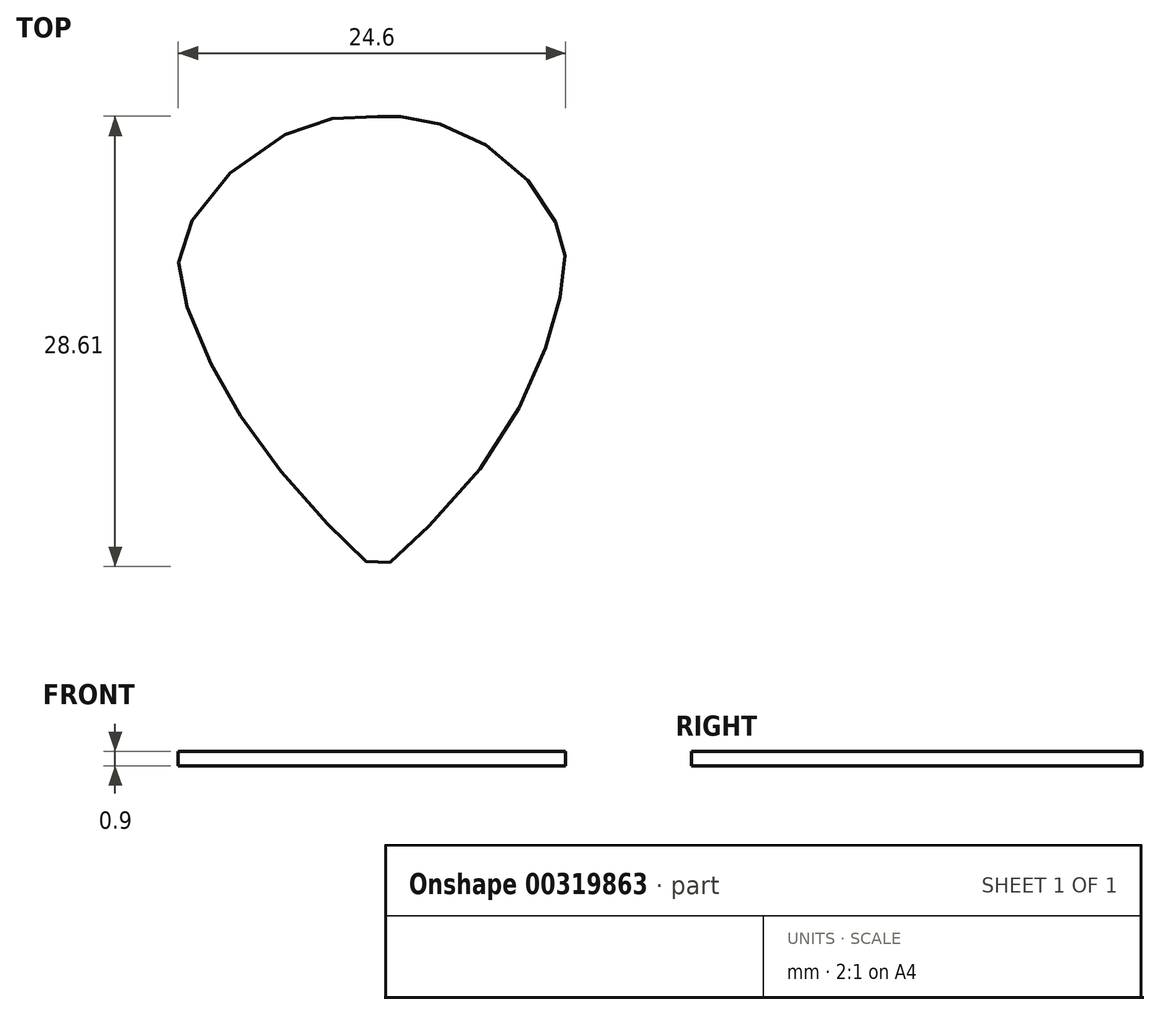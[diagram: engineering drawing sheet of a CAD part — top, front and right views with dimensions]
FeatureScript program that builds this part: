
annotation { "Feature Type Name" : "Feature", "Feature Type Description" : "" }
export const myFeature = defineFeature(function(context is Context, id is Id, definition is map)
    precondition{}
    {
        {
            var Q0;
            Q0=qCreatedBy(makeId("Top.planeOp"),FACE);
            var sketch = newSketch(context, id + "F0", { "sketchPlane" : qUnion([Q0])});
            skFitSpline(sketch, "E0", {"points": [v(0, 16.79) * mm, v(3.07, 16.79) * mm], "startDerivative": vector(3.07, 0) * mm, "endDerivative": vector(3.07, 0) * mm});
            skFitSpline(sketch, "E1", {"points": [v(0, 16.79) * mm, v(1.47, 16.79) * mm, v(2.93, 16.58) * mm, v(4.5, 16.12) * mm, v(6.77, 15.05) * mm, v(9.08, 13.24) * mm, v(10.58, 11.37) * mm, v(11.54, 9.58) * mm, v(11.8, 8.7) * mm, v(11.95, 7.34) * mm, v(11.67, 5.65) * mm, v(11.23, 3.75) * mm, v(9.95, 0.34) * mm, v(8.07, -3.36) * mm, v(4.7, -7.75) * mm, v(1.7, -10.68) * mm, v(0.56, -11.67) * mm, v(0, -11.79) * mm, v(-0.49, -11.63) * mm, v(-1.4, -10.86) * mm, v(-4.22, -7.96) * mm, v(-7.05, -4.55) * mm, v(-9.42, -1.1) * mm, v(-10.87, 1.7) * mm, v(-12.2, 5.04) * mm, v(-12.65, 6.96) * mm, v(-12.5, 8.35) * mm, v(-11.72, 10.31) * mm, v(-9.57, 12.98) * mm, v(-6.15, 15.5) * mm, v(-3.54, 16.47) * mm, v(-2.2, 16.79) * mm, v(0, 16.79) * mm]});
            skSolve(sketch);
        }
        {
            var Q0;
            Q0 = qSketchRegion(id + "F0", true);
            extrude(context, id + "F1", {"entities" : qUnion([Q0]), "depth" : 0.9 * mm});
        }
    });
